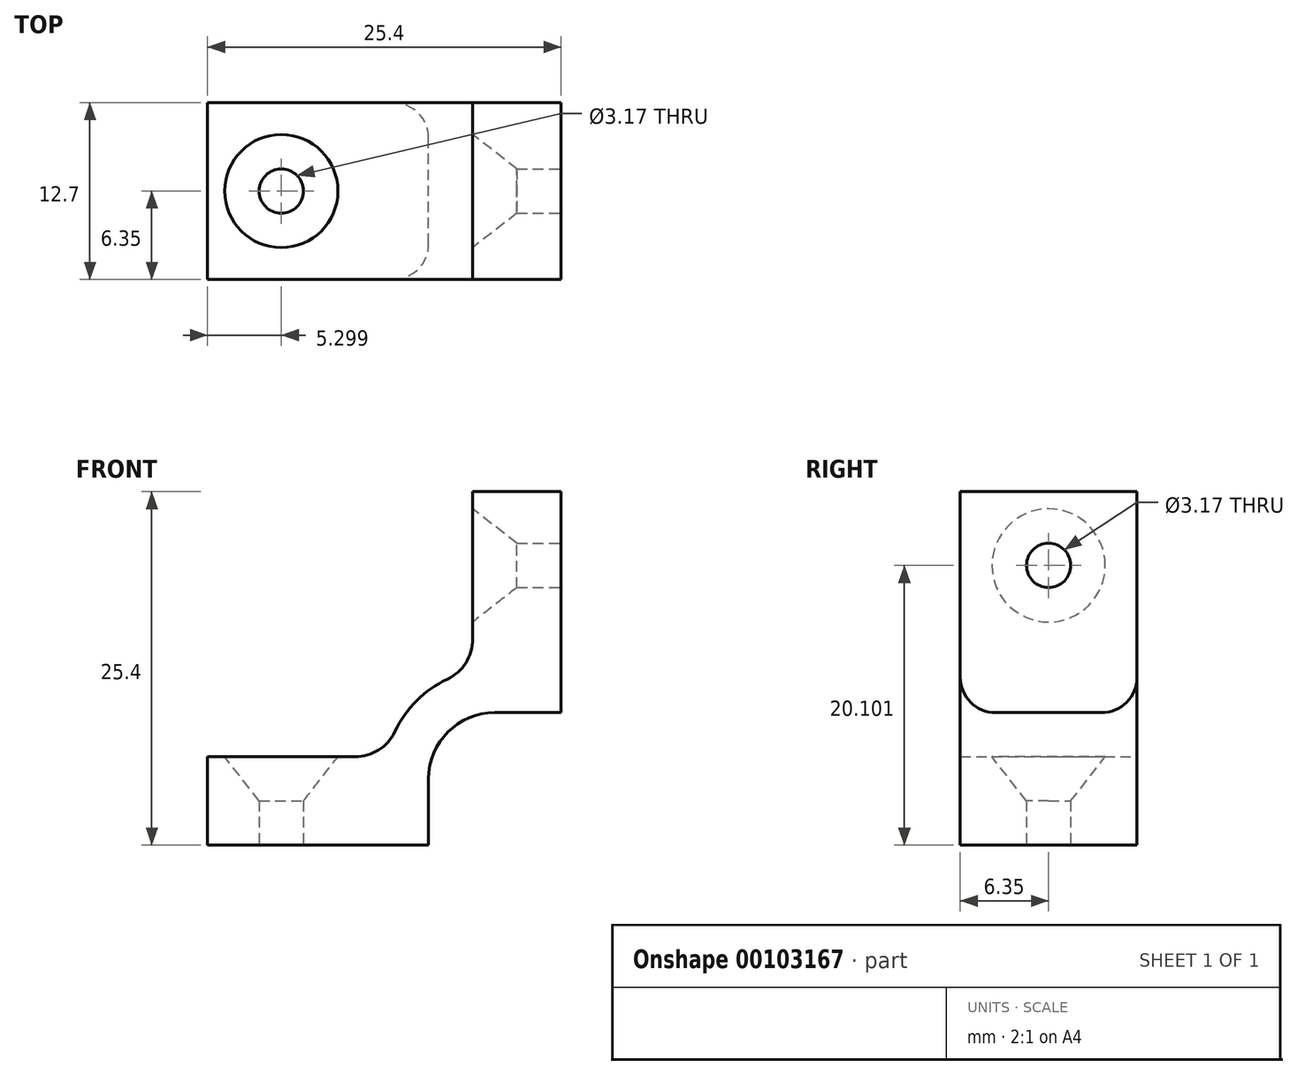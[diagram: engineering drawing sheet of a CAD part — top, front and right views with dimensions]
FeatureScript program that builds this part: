
annotation { "Feature Type Name" : "Feature", "Feature Type Description" : "" }
export const myFeature = defineFeature(function(context is Context, id is Id, definition is map)
    precondition{}
    {
        {
            var Q0;
            Q0=qCreatedBy(makeId("Front.planeOp"),FACE);
            var sketch = newSketch(context, id + "F0", { "sketchPlane" : qUnion([Q0])});
            skLineSegment(sketch, "E0", {"start": v(-88.82, 0) * mm, "end": v(35.12, 0) * mm, "construction": true});
            skLineSegment(sketch, "E1", {"start": v(0, 54.22) * mm, "end": v(0, -69.72) * mm, "construction": true});
            skArc(sketch, "E2", {"start": v(-4.76, 9.53) * mm, "mid": v(-8.13, 8.13) * mm, "end": v(-9.53, 4.76) * mm});
            skLineSegment(sketch, "E3", {"start": v(-4.76, 9.53) * mm, "end": v(0, 9.53) * mm});
            skLineSegment(sketch, "E4", {"start": v(0, 9.53) * mm, "end": v(0, 25.4) * mm});
            skLineSegment(sketch, "E5", {"start": v(0, 25.4) * mm, "end": v(-6.35, 25.4) * mm});
            skLineSegment(sketch, "E6", {"start": v(-6.35, 25.4) * mm, "end": v(-6.35, 14.8) * mm});
            skArc(sketch, "E7.0", {"start": v(-8.16, 11.93) * mm, "mid": v(-10.38, 10.38) * mm, "end": v(-11.93, 8.16) * mm});
            skLineSegment(sketch, "E8", {"start": v(-4.76, 4.76) * mm, "end": v(0, 0) * mm, "construction": true});
            skPoint(sketch, "E9.visualSharp", {"position": v(-6.35, 12.54) * mm});
            skArc(sketch, "E9.filletArc", {"start": v(-8.16, 11.93) * mm, "mid": v(-6.84, 13.1) * mm, "end": v(-6.35, 14.8) * mm});
            skArc(sketch, "E10.MirrorCS", {"start": v(-11.93, 8.16) * mm, "mid": v(-13.1, 6.84) * mm, "end": v(-14.8, 6.35) * mm});
            skLineSegment(sketch, "E11.MirrorCS", {"start": v(-25.4, 6.35) * mm, "end": v(-14.8, 6.35) * mm});
            skLineSegment(sketch, "E12.MirrorCS", {"start": v(-25.4, 0) * mm, "end": v(-25.4, 6.35) * mm});
            skLineSegment(sketch, "E13.MirrorCS", {"start": v(-9.53, 4.76) * mm, "end": v(-9.53, 0) * mm});
            skLineSegment(sketch, "E14", {"start": v(-25.4, 0) * mm, "end": v(-9.53, 0) * mm});
            skSolve(sketch);
        }
        {
            var Q0;
            Q0 = qSketchRegion(id + "F0", true);
            extrude(context, id + "F1", {"entities" : qUnion([Q0]), "endBound" : BoundingType.SYMMETRIC, "depth" : 12.7 * mm});
        }
        {
            var Q0;
            Q0=makeQuery(id+"F1.opExtrude","CAP_EDGE",EDGE,{"disambiguationData":[OSD([sQuery(id+"F0.wireOp",EDGE,"E3")])],"isStart":false});
            var Q1;
            Q1=makeQuery(id+"F1.opExtrude","CAP_EDGE",EDGE,{"disambiguationData":[OSD([sQuery(id+"F0.wireOp",EDGE,"E2")])],"isStart":true});
            fillet(context, id + "F2", {"entities" : qUnion([Q0, Q1]), "radius" : 2.54 * mm, "tangentPropagation" : true, "allowEdgeOverflow" : false});
        }
        {
            var Q0;
            Q0=qCreatedBy(makeId("Front.planeOp"),FACE);
            var sketch = newSketch(context, id + "F3", { "sketchPlane" : qUnion([Q0])});
            skLineSegment(sketch, "E15", {"start": v(-14.8, 6.35) * mm, "end": v(-25.4, 6.35) * mm, "construction": true});
            skLineSegment(sketch, "E16", {"start": v(-9.53, 0) * mm, "end": v(-25.4, 0) * mm, "construction": true});
            skLineSegment(sketch, "E17", {"start": v(-20.1, 6.35) * mm, "end": v(-20.1, 0) * mm, "construction": true});
            skLineSegment(sketch, "E18.right", {"start": v(-18.51, 0) * mm, "end": v(-18.51, 3.18) * mm});
            skLineSegment(sketch, "E19", {"start": v(-16.04, 6.35) * mm, "end": v(-18.51, 3.18) * mm});
            skLineSegment(sketch, "E20", {"start": v(-18.51, 0) * mm, "end": v(-20.1, 0) * mm});
            skLineSegment(sketch, "E21", {"start": v(-16.04, 6.35) * mm, "end": v(-13.2, 9.99) * mm});
            skLineSegment(sketch, "E22", {"start": v(-13.2, 9.99) * mm, "end": v(-20.1, 9.99) * mm});
            skLineSegment(sketch, "E23", {"start": v(-20.1, 9.99) * mm, "end": v(-20.1, 0) * mm});
            skSolve(sketch);
        }
        {
            var Q0;
            Q0 = qSketchRegion(id + "F3", true);
            var Q1;
            Q1=sQuery(id+"F3.wireOp",EDGE,"E17");
            revolve(context, id + "F4", {"operationType" : NewBodyOperationType.REMOVE, "entities" : qUnion([Q0]), "axis" : qUnion([Q1]), "revolveType" : RevolveType.ONE_DIRECTION, "oppositeDirection" : true, "angle" : 360 * degree});
        }
        {
            var Q0;
            Q0=qCreatedBy(makeId("Front.planeOp"),FACE);
            var sketch = newSketch(context, id + "F5", { "sketchPlane" : qUnion([Q0])});
            skLineSegment(sketch, "E24.0", {"start": v(-20.1, 9.99) * mm, "end": v(-20.1, 0) * mm, "construction": true});
            skLineSegment(sketch, "E25.0", {"start": v(-13.2, 9.99) * mm, "end": v(-20.1, 9.99) * mm, "construction": true});
            skLineSegment(sketch, "E26.0", {"start": v(-16.04, 6.35) * mm, "end": v(-13.2, 9.99) * mm, "construction": true});
            skLineSegment(sketch, "E27.0", {"start": v(-16.04, 6.35) * mm, "end": v(-18.51, 3.18) * mm, "construction": true});
            skLineSegment(sketch, "E28.0", {"start": v(-18.51, 0) * mm, "end": v(-18.51, 3.18) * mm, "construction": true});
            skLineSegment(sketch, "E29.0", {"start": v(-18.51, 0) * mm, "end": v(-20.1, 0) * mm, "construction": true});
            skLineSegment(sketch, "E30.MirrorCS", {"start": v(-6.35, 16.04) * mm, "end": v(-9.99, 13.2) * mm});
            skLineSegment(sketch, "E31.MirrorCS", {"start": v(-9.99, 13.2) * mm, "end": v(-9.99, 20.1) * mm});
            skLineSegment(sketch, "E32.MirrorCS", {"start": v(-9.99, 20.1) * mm, "end": v(0, 20.1) * mm});
            skLineSegment(sketch, "E33.MirrorCS", {"start": v(0, 18.51) * mm, "end": v(-3.18, 18.51) * mm});
            skLineSegment(sketch, "E34.MirrorCS", {"start": v(0, 18.51) * mm, "end": v(0, 20.1) * mm, "construction": true});
            skLineSegment(sketch, "E35.MirrorCS", {"start": v(-6.35, 16.04) * mm, "end": v(-3.18, 18.51) * mm});
            skLineSegment(sketch, "E36", {"start": v(0, 20.1) * mm, "end": v(0, 18.51) * mm});
            skSolve(sketch);
        }
        {
            var Q0;
            Q0 = qSketchRegion(id + "F5", true);
            var Q1;
            Q1=sQuery(id+"F5.wireOp",EDGE,"E32.MirrorCS");
            revolve(context, id + "F6", {"operationType" : NewBodyOperationType.REMOVE, "entities" : qUnion([Q0]), "axis" : qUnion([Q1]), "revolveType" : RevolveType.FULL, "oppositeDirection" : true});
        }
    });
